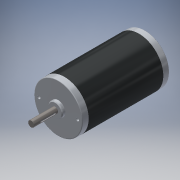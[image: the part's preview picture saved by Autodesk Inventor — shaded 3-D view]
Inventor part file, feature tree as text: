
AUTODESK INVENTOR PART (.ipt)
format: ipt  version: 2017 SP1 (Build 210196100, 196)  size: 167,424 bytes
history: native  units: in
note: dims shown in document units (in); Inventor stores cm internally (conversion verified against a paired STEP export)
features: fillet x1
ambient origin geometry x8: Origin, YZ Plane, XZ Plane, XY Plane, X Axis, Y Axis, Z Axis, Center Point
bodies: Solid1 (feature_tree)
feature tree (1):
  fillet  "Fillet5"  [1 undecoded]
note: 1 required parameter value undecoded (feature->parameter linkage not recoverable at this tier; creation-order binding heuristic only, values carry confidence <= 0.55)
